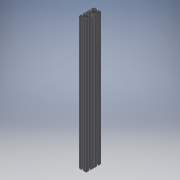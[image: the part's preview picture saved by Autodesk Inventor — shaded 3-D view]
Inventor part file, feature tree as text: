
AUTODESK INVENTOR PART (.ipt)
format: ipt  version: 2018 (Build 220112000, 112)  size: 636,928 bytes
history: native  units: mm
features: other x1, extrude x1, sketch x1
ambient origin geometry x8: Origin, YZ Plane, XZ Plane, XY Plane, X Axis, Y Axis, Z Axis, Center Point
bodies: Body1 (feature_tree)
feature tree (3):
  other  "Sólido1"
  extrude  "Extrusão1"  [1 undecoded]
  sketch  "Esboço1"  dims[d0=700.0mm d1=0.0mm]
note: 1 required parameter value undecoded (feature->parameter linkage not recoverable at this tier; creation-order binding heuristic only, values carry confidence <= 0.55)
